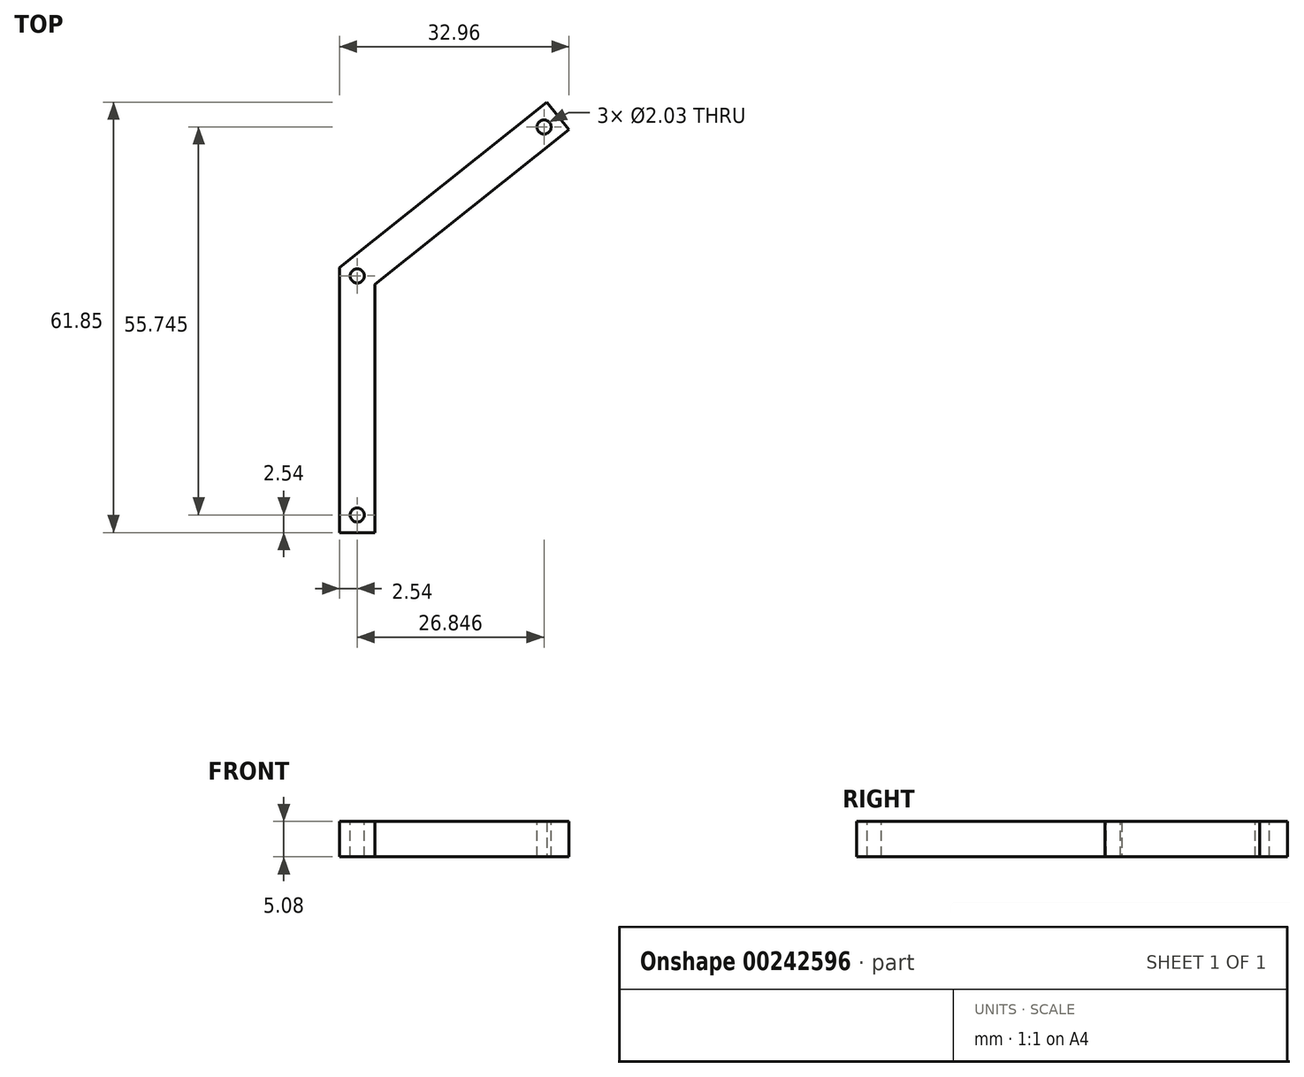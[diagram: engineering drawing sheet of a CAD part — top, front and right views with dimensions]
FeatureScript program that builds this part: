
annotation { "Feature Type Name" : "Feature", "Feature Type Description" : "" }
export const myFeature = defineFeature(function(context is Context, id is Id, definition is map)
    precondition{}
    {
        {
            var Q0;
            Q0=qCreatedBy(makeId("Top.planeOp"),FACE);
            var sketch = newSketch(context, id + "F0", { "sketchPlane" : qUnion([Q0])});
            skLineSegment(sketch, "E0", {"start": v(0, 0) * mm, "end": v(0, -38.1) * mm});
            skLineSegment(sketch, "E1", {"start": v(0, -38.1) * mm, "end": v(5.08, -38.1) * mm});
            skLineSegment(sketch, "E2", {"start": v(5.08, -38.1) * mm, "end": v(5.08, -2.45) * mm});
            skLineSegment(sketch, "E3", {"start": v(5.08, -2.45) * mm, "end": v(32.96, 19.78) * mm});
            skLineSegment(sketch, "E4", {"start": v(32.96, 19.78) * mm, "end": v(29.79, 23.75) * mm});
            skLineSegment(sketch, "E5", {"start": v(29.79, 23.75) * mm, "end": v(0, 0) * mm});
            skSolve(sketch);
        }
        {
            var Q0;
            Q0 = qSketchRegion(id + "F0", true);
            extrude(context, id + "F1", {"entities" : qUnion([Q0]), "depth" : 5.08 * mm});
        }
        {
            var Q0;
            Q0=makeQuery(id+"F1.opExtrude","CAP_FACE",FACE,{"disambiguationData":[OSD([sQuery(id+"F0.wireOp",EDGE,"E0"),sQuery(id+"F0.wireOp",EDGE,"E1"),sQuery(id+"F0.wireOp",EDGE,"E2"),sQuery(id+"F0.wireOp",EDGE,"E3"),sQuery(id+"F0.wireOp",EDGE,"E4"),sQuery(id+"F0.wireOp",EDGE,"E5")])],"isStart":false});
            var sketch = newSketch(context, id + "F2", { "sketchPlane" : qUnion([Q0])});
            skLineSegment(sketch, "E6", {"start": v(5.08, -2.45) * mm, "end": v(0, 0) * mm, "construction": true});
            skCircle(sketch, "E7", {"center": v(2.54, -1.22) * mm, "radius": 1.02 * mm});
            skCircle(sketch, "E8", {"center": v(2.54, -35.56) * mm, "radius": 1.02 * mm});
            skPoint(sketch, "E8.centerSnap0", {"position": v(2.54, -38.1) * mm});
            skCircle(sketch, "E9", {"center": v(29.39, 20.19) * mm, "radius": 1.02 * mm});
            skSolve(sketch);
        }
        {
            var Q0;
            Q0 = qSketchRegion(id + "F2", true);
            extrude(context, id + "F3", {"entities" : qUnion([Q0]), "operationType" : NewBodyOperationType.REMOVE, "endBound" : BoundingType.THROUGH_ALL, "oppositeDirection" : true, "depth" : 25.4 * mm});
        }
    });
